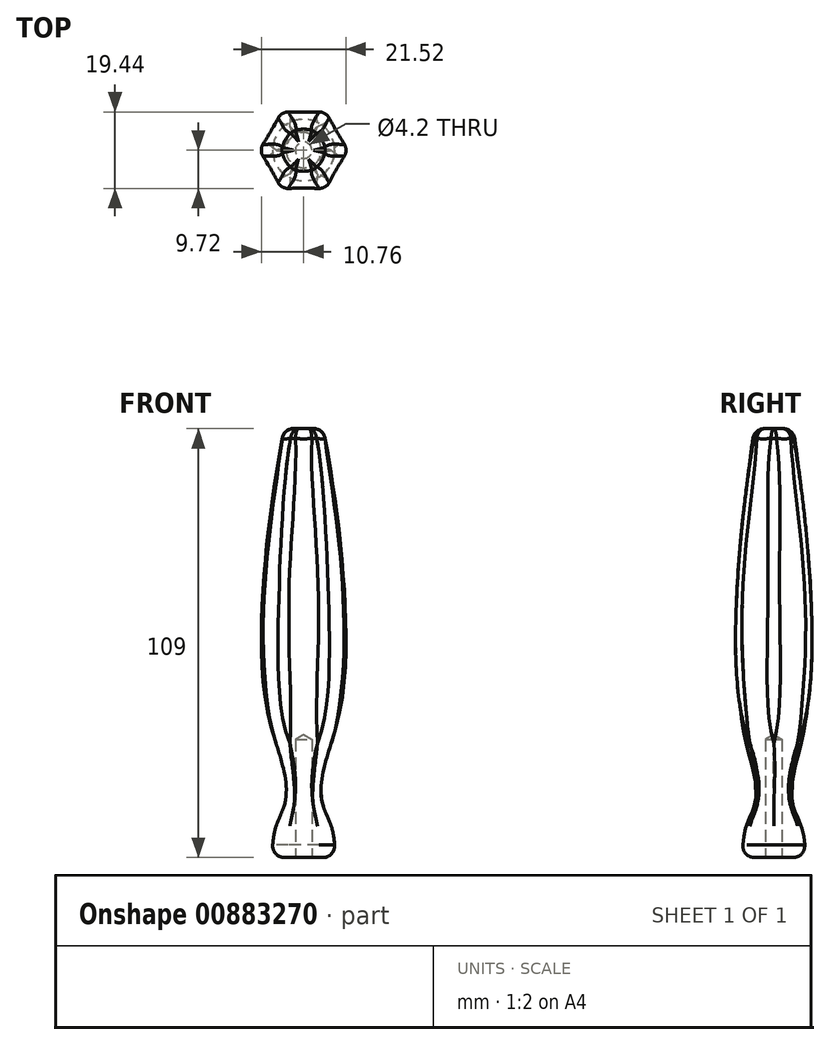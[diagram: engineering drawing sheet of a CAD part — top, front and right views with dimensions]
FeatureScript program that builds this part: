
annotation { "Feature Type Name" : "Feature", "Feature Type Description" : "" }
export const myFeature = defineFeature(function(context is Context, id is Id, definition is map)
    precondition{}
    {
        {
            var Q0;
            Q0=qCreatedBy(makeId("Top.planeOp"),FACE);
            var sketch = newSketch(context, id + "F0", { "sketchPlane" : qUnion([Q0])});
            skCircle(sketch, "E0", {"center": v(0, 0) * mm, "radius": 7 * mm});
            skSolve(sketch);
        }
        {
            var Q0;
            Q0=qCreatedBy(makeId("Top.planeOp"),FACE);
            cPlane(context, id + "F1", {"entities" : qUnion([Q0]), "cplaneType" : CPlaneType.OFFSET, "offset" : 5 * mm, "width" : 150 * mm, "height" : 150 * mm});
        }
        {
            var Q0;
            Q0=qCreatedBy(id+"F1.planeOp",FACE);
            cPlane(context, id + "F2", {"entities" : qUnion([Q0]), "cplaneType" : CPlaneType.OFFSET, "offset" : 16 * mm, "width" : 150 * mm, "height" : 150 * mm});
        }
        {
            var Q0;
            Q0=qCreatedBy(id+"F2.planeOp",FACE);
            var sketch = newSketch(context, id + "F3", { "sketchPlane" : qUnion([Q0])});
            skCircle(sketch, "E1", {"center": v(0, 0) * mm, "radius": 7 * mm});
            skSolve(sketch);
        }
        {
            var Q0;
            Q0=qCreatedBy(id+"F2.planeOp",FACE);
            cPlane(context, id + "F4", {"entities" : qUnion([Q0]), "cplaneType" : CPlaneType.OFFSET, "offset" : 10 * mm, "width" : 150 * mm, "height" : 150 * mm});
        }
        {
            var Q0;
            Q0=qCreatedBy(id+"F4.planeOp",FACE);
            var sketch = newSketch(context, id + "F5", { "sketchPlane" : qUnion([Q0])});
            skCircle(sketch, "E2.cCircle", {"center": v(0, 0) * mm, "radius": 10 * mm, "construction": true});
            skLineSegment(sketch, "E2.0", {"start": v(5, -8.66) * mm, "end": v(-5, -8.66) * mm});
            skLineSegment(sketch, "E2.1", {"start": v(-5, -8.66) * mm, "end": v(-10, 0) * mm});
            skLineSegment(sketch, "E2.2", {"start": v(-10, 0) * mm, "end": v(-5, 8.66) * mm});
            skLineSegment(sketch, "E2.3", {"start": v(-5, 8.66) * mm, "end": v(5, 8.66) * mm});
            skLineSegment(sketch, "E2.4", {"start": v(5, 8.66) * mm, "end": v(10, 0) * mm});
            skLineSegment(sketch, "E2.5", {"start": v(10, 0) * mm, "end": v(5, -8.66) * mm});
            skSolve(sketch);
        }
        {
            var Q0;
            Q0=qCreatedBy(id+"F4.planeOp",FACE);
            cPlane(context, id + "F6", {"entities" : qUnion([Q0]), "cplaneType" : CPlaneType.OFFSET, "offset" : 25 * mm, "width" : 150 * mm, "height" : 150 * mm});
        }
        {
            var Q0;
            Q0=qCreatedBy(id+"F6.planeOp",FACE);
            var sketch = newSketch(context, id + "F7", { "sketchPlane" : qUnion([Q0])});
            skCircle(sketch, "E3.cCircle", {"center": v(0, 0) * mm, "radius": 11 * mm, "construction": true});
            skLineSegment(sketch, "E3.0", {"start": v(11, 0) * mm, "end": v(5.5, -9.53) * mm});
            skLineSegment(sketch, "E3.1", {"start": v(5.5, -9.53) * mm, "end": v(-5.5, -9.53) * mm});
            skLineSegment(sketch, "E3.2", {"start": v(-5.5, -9.53) * mm, "end": v(-11, 0) * mm});
            skLineSegment(sketch, "E3.3", {"start": v(-11, 0) * mm, "end": v(-5.5, 9.53) * mm});
            skLineSegment(sketch, "E3.4", {"start": v(-5.5, 9.53) * mm, "end": v(5.5, 9.53) * mm});
            skLineSegment(sketch, "E3.5", {"start": v(5.5, 9.53) * mm, "end": v(11, 0) * mm});
            skSolve(sketch);
        }
        {
            var Q0;
            Q0=qCreatedBy(id+"F6.planeOp",FACE);
            cPlane(context, id + "F8", {"entities" : qUnion([Q0]), "cplaneType" : CPlaneType.OFFSET, "offset" : 30 * mm, "width" : 150 * mm, "height" : 150 * mm});
        }
        {
            var Q0;
            Q0=qCreatedBy(id+"F8.planeOp",FACE);
            var sketch = newSketch(context, id + "F9", { "sketchPlane" : qUnion([Q0])});
            skCircle(sketch, "E4.cCircle", {"center": v(0, 0) * mm, "radius": 8 * mm, "construction": true});
            skLineSegment(sketch, "E4.0", {"start": v(8, 0) * mm, "end": v(4, -6.93) * mm});
            skLineSegment(sketch, "E4.1", {"start": v(4, -6.93) * mm, "end": v(-4, -6.93) * mm});
            skLineSegment(sketch, "E4.2", {"start": v(-4, -6.93) * mm, "end": v(-8, 0) * mm});
            skLineSegment(sketch, "E4.3", {"start": v(-8, 0) * mm, "end": v(-4, 6.93) * mm});
            skLineSegment(sketch, "E4.4", {"start": v(-4, 6.93) * mm, "end": v(4, 6.93) * mm});
            skLineSegment(sketch, "E4.5", {"start": v(4, 6.93) * mm, "end": v(8, 0) * mm});
            skSolve(sketch);
        }
        {
            var Q0;
            Q0=qCreatedBy(id+"F8.planeOp",FACE);
            cPlane(context, id + "F10", {"entities" : qUnion([Q0]), "cplaneType" : CPlaneType.OFFSET, "offset" : 15 * mm, "width" : 150 * mm, "height" : 150 * mm});
        }
        {
            var Q0;
            Q0=qCreatedBy(id+"F10.planeOp",FACE);
            var sketch = newSketch(context, id + "F11", { "sketchPlane" : qUnion([Q0])});
            skCircle(sketch, "E5", {"center": v(0, 0) * mm, "radius": 5 * mm});
            skSolve(sketch);
        }
        {
            var Q0;
            Q0=qCreatedBy(makeId("Top.planeOp"),FACE);
            cPlane(context, id + "F12", {"entities" : qUnion([Q0]), "cplaneType" : CPlaneType.OFFSET, "offset" : 8 * mm, "oppositeDirection" : true, "width" : 150 * mm, "height" : 150 * mm});
        }
        {
            var Q0;
            Q0=qCreatedBy(id+"F12.planeOp",FACE);
            var sketch = newSketch(context, id + "F13", { "sketchPlane" : qUnion([Q0])});
            skCircle(sketch, "E6", {"center": v(0, 0) * mm, "radius": 8 * mm});
            skSolve(sketch);
        }
        {
            var Q0;
            Q0=qCreatedBy(id+"F1.planeOp",FACE);
            var sketch = newSketch(context, id + "F14", { "sketchPlane" : qUnion([Q0])});
            skCircle(sketch, "E7", {"center": v(0, 0) * mm, "radius": 5 * mm});
            skSolve(sketch);
        }
        {
            var Q0;
            Q0=makeQuery(id+"F13.imprint","IMPRINT",FACE,{"disambiguationData":[TD([[makeQuery(id+"F13.imprint","IMPRINT",EDGE,{"derivedFrom":sQuery(id+"F13.wireOp",EDGE,"E6")}),1.0]])]});
            var Q1;
            Q1=makeQuery(id+"F0.imprint","IMPRINT",FACE,{"disambiguationData":[TD([[makeQuery(id+"F0.imprint","IMPRINT",EDGE,{"derivedFrom":sQuery(id+"F0.wireOp",EDGE,"E0")}),1.0]])]});
            var Q2;
            Q2=makeQuery(id+"F14.imprint","IMPRINT",FACE,{"disambiguationData":[TD([[makeQuery(id+"F14.imprint","IMPRINT",EDGE,{"derivedFrom":sQuery(id+"F14.wireOp",EDGE,"E7")}),1.0]])]});
            var Q3;
            Q3=makeQuery(id+"F3.imprint","IMPRINT",FACE,{"disambiguationData":[TD([[makeQuery(id+"F3.imprint","IMPRINT",EDGE,{"derivedFrom":sQuery(id+"F3.wireOp",EDGE,"E1")}),1.0]])]});
            var Q4;
            Q4=makeQuery(id+"F5.imprint","IMPRINT",FACE,{"disambiguationData":[TD([[makeQuery(id+"F5.imprint","IMPRINT",EDGE,{"derivedFrom":sQuery(id+"F5.wireOp",EDGE,"E2.0")}),-1.0]])]});
            var Q5;
            Q5=makeQuery(id+"F7.imprint","IMPRINT",FACE,{"disambiguationData":[TD([[makeQuery(id+"F7.imprint","IMPRINT",EDGE,{"derivedFrom":sQuery(id+"F7.wireOp",EDGE,"E3.0")}),-1.0]])]});
            var Q6;
            Q6=makeQuery(id+"F9.imprint","IMPRINT",FACE,{"disambiguationData":[TD([[makeQuery(id+"F9.imprint","IMPRINT",EDGE,{"derivedFrom":sQuery(id+"F9.wireOp",EDGE,"E4.0")}),-1.0]])]});
            var Q7;
            Q7=makeQuery(id+"F11.imprint","IMPRINT",FACE,{"disambiguationData":[TD([[makeQuery(id+"F11.imprint","IMPRINT",EDGE,{"derivedFrom":sQuery(id+"F11.wireOp",EDGE,"E5")}),1.0]])]});
            loft(context, id + "F15", {"sheetProfilesArray" : [{ "sheetProfileEntities" : qUnion([Q0]) }, { "sheetProfileEntities" : qUnion([Q1]) }, { "sheetProfileEntities" : qUnion([Q2]) }, { "sheetProfileEntities" : qUnion([Q3]) }, { "sheetProfileEntities" : qUnion([Q4]) }, { "sheetProfileEntities" : qUnion([Q5]) }, { "sheetProfileEntities" : qUnion([Q6]) }, { "sheetProfileEntities" : qUnion([Q7]) }]});
        }
        {
            var Q0;
            Q0=makeQuery(id+"F15.opLoft","CAP_FACE",FACE,{"disambiguationData":[OSD([makeQuery(id+"F13.imprint","IMPRINT",FACE,{"disambiguationData":[TD([[makeQuery(id+"F13.imprint","IMPRINT",EDGE,{"derivedFrom":sQuery(id+"F13.wireOp",EDGE,"E6")}),1.0]])]})])],"isStart":true});
            fillet(context, id + "F16", {"entities" : qUnion([Q0]), "radius" : 3 * mm, "tangentPropagation" : true, "allowEdgeOverflow" : false});
        }
        {
            var Q0;
            Q0=makeQuery(id+"F15.opLoft","CAP_FACE",FACE,{"disambiguationData":[OSD([makeQuery(id+"F11.imprint","IMPRINT",FACE,{"disambiguationData":[TD([[makeQuery(id+"F11.imprint","IMPRINT",EDGE,{"derivedFrom":sQuery(id+"F11.wireOp",EDGE,"E5")}),1.0]])]})])],"isStart":true});
            var Q1;
            Q1=makeQuery(id+"F15.opLoft","SWEPT_FACE",FACE,{"disambiguationData":[OSD([sQuery(id+"F0.wireOp",EDGE,"E0"),sQuery(id+"F3.wireOp",EDGE,"E1"),sQuery(id+"F5.wireOp",EDGE,"E2.0"),sQuery(id+"F5.wireOp",EDGE,"E2.4"),sQuery(id+"F5.wireOp",EDGE,"E2.5"),sQuery(id+"F7.wireOp",EDGE,"E3.0"),sQuery(id+"F7.wireOp",EDGE,"E3.1"),sQuery(id+"F7.wireOp",EDGE,"E3.5"),sQuery(id+"F9.wireOp",EDGE,"E4.0"),sQuery(id+"F9.wireOp",EDGE,"E4.1"),sQuery(id+"F9.wireOp",EDGE,"E4.5"),sQuery(id+"F11.wireOp",EDGE,"E5"),sQuery(id+"F13.wireOp",EDGE,"E6"),sQuery(id+"F14.wireOp",EDGE,"E7")])]});
            var Q2;
            Q2=makeQuery(id+"F15.opLoft","SWEPT_FACE",FACE,{"disambiguationData":[OSD([sQuery(id+"F0.wireOp",EDGE,"E0"),sQuery(id+"F3.wireOp",EDGE,"E1"),sQuery(id+"F5.wireOp",EDGE,"E2.0"),sQuery(id+"F5.wireOp",EDGE,"E2.1"),sQuery(id+"F5.wireOp",EDGE,"E2.2"),sQuery(id+"F5.wireOp",EDGE,"E2.5"),sQuery(id+"F7.wireOp",EDGE,"E3.0"),sQuery(id+"F7.wireOp",EDGE,"E3.1"),sQuery(id+"F7.wireOp",EDGE,"E3.2"),sQuery(id+"F9.wireOp",EDGE,"E4.0"),sQuery(id+"F9.wireOp",EDGE,"E4.1"),sQuery(id+"F9.wireOp",EDGE,"E4.2"),sQuery(id+"F11.wireOp",EDGE,"E5"),sQuery(id+"F13.wireOp",EDGE,"E6"),sQuery(id+"F14.wireOp",EDGE,"E7")])]});
            var Q3;
            Q3=makeQuery(id+"F15.opLoft","SWEPT_FACE",FACE,{"disambiguationData":[OSD([sQuery(id+"F0.wireOp",EDGE,"E0"),sQuery(id+"F3.wireOp",EDGE,"E1"),sQuery(id+"F5.wireOp",EDGE,"E2.0"),sQuery(id+"F5.wireOp",EDGE,"E2.3"),sQuery(id+"F5.wireOp",EDGE,"E2.4"),sQuery(id+"F5.wireOp",EDGE,"E2.5"),sQuery(id+"F7.wireOp",EDGE,"E3.0"),sQuery(id+"F7.wireOp",EDGE,"E3.4"),sQuery(id+"F7.wireOp",EDGE,"E3.5"),sQuery(id+"F9.wireOp",EDGE,"E4.0"),sQuery(id+"F9.wireOp",EDGE,"E4.4"),sQuery(id+"F9.wireOp",EDGE,"E4.5"),sQuery(id+"F11.wireOp",EDGE,"E5"),sQuery(id+"F13.wireOp",EDGE,"E6"),sQuery(id+"F14.wireOp",EDGE,"E7")])]});
            var Q4;
            Q4=makeQuery(id+"F15.opLoft","SWEPT_FACE",FACE,{"disambiguationData":[OSD([sQuery(id+"F0.wireOp",EDGE,"E0"),sQuery(id+"F3.wireOp",EDGE,"E1"),sQuery(id+"F5.wireOp",EDGE,"E2.0"),sQuery(id+"F5.wireOp",EDGE,"E2.1"),sQuery(id+"F5.wireOp",EDGE,"E2.2"),sQuery(id+"F5.wireOp",EDGE,"E2.3"),sQuery(id+"F7.wireOp",EDGE,"E3.1"),sQuery(id+"F7.wireOp",EDGE,"E3.2"),sQuery(id+"F7.wireOp",EDGE,"E3.3"),sQuery(id+"F9.wireOp",EDGE,"E4.1"),sQuery(id+"F9.wireOp",EDGE,"E4.2"),sQuery(id+"F9.wireOp",EDGE,"E4.3"),sQuery(id+"F11.wireOp",EDGE,"E5"),sQuery(id+"F13.wireOp",EDGE,"E6"),sQuery(id+"F14.wireOp",EDGE,"E7")])]});
            var Q5;
            Q5=makeQuery(id+"F15.opLoft","SWEPT_FACE",FACE,{"disambiguationData":[OSD([sQuery(id+"F0.wireOp",EDGE,"E0"),sQuery(id+"F3.wireOp",EDGE,"E1"),sQuery(id+"F5.wireOp",EDGE,"E2.1"),sQuery(id+"F5.wireOp",EDGE,"E2.2"),sQuery(id+"F5.wireOp",EDGE,"E2.3"),sQuery(id+"F5.wireOp",EDGE,"E2.4"),sQuery(id+"F7.wireOp",EDGE,"E3.2"),sQuery(id+"F7.wireOp",EDGE,"E3.3"),sQuery(id+"F7.wireOp",EDGE,"E3.4"),sQuery(id+"F9.wireOp",EDGE,"E4.2"),sQuery(id+"F9.wireOp",EDGE,"E4.3"),sQuery(id+"F9.wireOp",EDGE,"E4.4"),sQuery(id+"F11.wireOp",EDGE,"E5"),sQuery(id+"F13.wireOp",EDGE,"E6"),sQuery(id+"F14.wireOp",EDGE,"E7")])]});
            fillet(context, id + "F17", {"entities" : qUnion([Q0, Q1, Q2, Q3, Q4, Q5]), "radius" : 3 * mm, "tangentPropagation" : true, "allowEdgeOverflow" : false});
        }
        {
            var Q0;
            Q0=makeQuery(id+"F15.opLoft","CAP_FACE",FACE,{"disambiguationData":[OSD([makeQuery(id+"F13.imprint","IMPRINT",FACE,{"disambiguationData":[TD([[makeQuery(id+"F13.imprint","IMPRINT",EDGE,{"derivedFrom":sQuery(id+"F13.wireOp",EDGE,"E6")}),1.0]])]})])],"isStart":true});
            var sketch = newSketch(context, id + "F18", { "sketchPlane" : qUnion([Q0])});
            skPoint(sketch, "E8", {"position": v(0, 0) * mm});
            skSolve(sketch);
        }
        {
            var Q0;
            Q0=sQuery(id+"F18.wireOp",VERTEX,"E8");
            var Q1;
            Q1=makeQuery(id+"F15.opLoft","SWEPT_BODY",BODY,{"disambiguationData":[OSD([sQuery(id+"F0.wireOp",EDGE,"E0"),sQuery(id+"F3.wireOp",EDGE,"E1"),sQuery(id+"F5.wireOp",EDGE,"E2.5"),sQuery(id+"F7.wireOp",EDGE,"E3.5"),sQuery(id+"F9.wireOp",EDGE,"E4.5"),makeQuery(id+"F11.imprint","IMPRINT",FACE,{"disambiguationData":[TD([[makeQuery(id+"F11.imprint","IMPRINT",EDGE,{"derivedFrom":sQuery(id+"F11.wireOp",EDGE,"E5")}),1.0]])]}),makeQuery(id+"F13.imprint","IMPRINT",FACE,{"disambiguationData":[TD([[makeQuery(id+"F13.imprint","IMPRINT",EDGE,{"derivedFrom":sQuery(id+"F13.wireOp",EDGE,"E6")}),1.0]])]}),sQuery(id+"F14.wireOp",EDGE,"E7")])]});
            hole(context, id + "F19", {"style" : HoleStyle.SIMPLE, "endStyle" : HoleEndStyle.BLIND, "standardTappedOrClearance" : lookupTablePath({ "standard" : "ISO", "engagement" : "75%", "pitch" : "0.8 mm", "size" : "M5", "type" : "Tapped" }), "standardBlindInLast" : lookupTablePath({ "standard" : "ISO", "engagement" : "75%", "pitch" : "0.8 mm", "size" : "M5", "type" : "Tapped" }), "holeDiameter" : 4.2 * mm, "majorDiameter" : 5 * mm, "showTappedDepth" : true, "holeDepth" : 30 * mm, "isTappedThrough" : true, "tappedDepth" : 27.6 * mm, "tapClearance" : 3, "locations" : qUnion([Q0]), "scope" : qUnion([Q1])});
        }
    });
